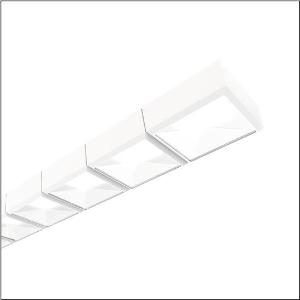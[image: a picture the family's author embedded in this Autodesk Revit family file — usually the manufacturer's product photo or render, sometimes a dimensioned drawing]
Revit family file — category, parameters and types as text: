
# Revit family: scriptus_r__11_5mz223d04wa_758a
name_source: partatom
category: Lighting Fixtures
units: mm (PartAtom-declared; Revit-internal decimal feet)

## family parameters
Cut with Voids When Loaded = No
Host = Face
Light Source = No
Part Type = Normal
Room Calculation Point = No
Round Connector Dimension = Use Diameter
Shared = No

## types (1)
- --- (1 x LED 4000K / CRI = 80 (unbekannt), 7230 lm, 4000K)
    Apparent Load = 51 VA
    CIE Flux Codes = 82 95 99 100 100
    Color Rendering = 80
    Color Temperature = 4000K
    Default Elevation = 1800 mm
    Description = Scriptus® 11, office luminaire, primary optical cover: lenses, CAT 2 (L<= 3000cd/m²), light emission: direct distribution, primary light characteristic: symmetric, installation type: surface-mounted, LED, rated luminous flux: 7.230lm, luminous efficacy: 143lm/W, light colour: 840, colour temperature: 4000K, control gear: ECG DALI, with terminal, 5-pole, mains connection: 230V, AC, 50Hz, rated input power: 51W, housing, luminaire housing, of aluminium, traffic white (RAL 9016), length: 2.426mm, width: 114mm, height: 57mm, protection rating (complete): IP20, insulation class (complete): insulation class I (protective earthing), certification: CE, ENEC, VDE, protection symbol: F, permissible operating ambient temperature: 0..+35°C, standard: EN 50419, packaging unit: 1 piece
    Height = 57 mm
    Lamp = 1 x LED 4000K / CRI >= 80 (unbekannt)
    Lamp Light Flux = 7230 lm
    Lamp count = 1
    Length = 2426 mm
    Luminous efficacy = 143 lm/W
    Manufacturer = Siteco
    ModVariant = No
    Model = 5MZ223D04WA
    Mounting Place = Ceiling
    Mounting Type = Surface mounted
    Number of Poles = 1
    OnlyDefault = Yes
    Power Factor = 1
    Product Name = Scriptus® 11
    Product group = office luminaire | ceiling mounted
    ProductGroupID = 300
    Protection Class = Protection class I
    Protection Degree = IP 20
    RLX_Detail_Level = 1
    RLX_Emergency_Light_Flux = 0 lm
    RLX_Emergency_Type = 0
    RLX_Emergency_Type_DB = No
    RlxData = <blob elided: 31317 chars, md5=f8b4da32>
    Socket = socket
    Standby Power = 0 W
    System Light Flux = 7230 lm
    System Power = 51 W
    Type Comments = factory setting: luminous flux: 100 % | dim-lin: 254 | 525 mA
    Type Image = l_1004833.jpg
    URL = http://relux.com
    VarID = @adj_164809
    Voltage = 0 V
    Weight = 0.00 kg
    Width = 114 mm

## geometry (parser evidence)
native form markers: Blend x4, Sweep x9
no freeform markers — native parametric forms only
